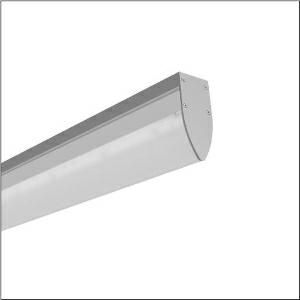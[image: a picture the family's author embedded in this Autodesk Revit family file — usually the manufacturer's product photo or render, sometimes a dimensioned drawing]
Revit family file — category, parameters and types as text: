
# Revit family: mira_r__21_td_51fr527d424a_f4a9
name_source: partatom
category: Lighting Fixtures
units: mm (PartAtom-declared; Revit-internal decimal feet)

## family parameters
Cut with Voids When Loaded = No
Host = Face
Light Source = No
Part Type = Normal
Room Calculation Point = No
Round Connector Dimension = Use Diameter
Shared = No

## types (1)
- Mira® 21 TD (1 x LED, 2020 lm, 14 W, 4000K)
    Apparent Load = 14 VA
    CIE Flux Codes = 40 68 87 81 100
    Color Rendering = 80
    Color Temperature = 4000K
    Default Elevation = 1800 mm
    Description = Mira® 21 TD, clean room luminaire, primary light control with reflector, primary optical cover: cover, of PMMA, frosted, light emission: direct distribution, primary light characteristic: symmetric, installation type: surface-mounted, LED, rated luminous flux: 2.020lm, luminous efficacy: 144lm/W, light colour: 840, colour temperature: 4000K, control gear: ON/OFF, with terminal, 3-pole, max. 2.5mm², mains connection: 230V, AC, 50/60Hz, rated input power: 14W, luminaire housing, of sheet steel, coated, pure white (RAL 9010), length: 600mm, width: 55mm, height: 120mm, protection rating (complete): IP43, insulation class (complete): insulation class I (protective earthing), certification: CE, UKCA, permissible operating ambient temperature: -5..+40°C, standard: EN 50419, packaging unit: 1 piece
    Height = 120 mm
    Lamp = 1 x LED
    Lamp Light Flux = 2020 lm
    Lamp Power = 14 W
    Lamp count = 1
    Length = 600 mm
    Luminous efficacy = 144 lm/W
    Manufacturer = Siteco
    ModVariant = No
    Model = 51FR527D424A
    Mounting Place = Ceiling
    Mounting Type = Surface mounted
    Number of Poles = 1
    OnlyDefault = Yes
    Power Factor = 1
    Product Name = Mira® 21 TD
    Product group = clean room luminaire | ceiling mounted
    ProductGroupID = 305
    Protection Class = Protection class I
    Protection Degree = IP 43
    RLX_Detail_Level = 1
    RLX_Emergency_Light_Flux = 0 lm
    RLX_Emergency_Type = 0
    RLX_Emergency_Type_DB = No
    RlxData = <blob elided: 25869 chars, md5=cd2b4e9b>
    Socket = socket
    Standby Power = 0 W
    System Light Flux = 2020 lm
    System Power = 14 W
    Type Comments = Product without accessories
    Type Image = l_1007115.jpg
    URL = http://relux.com
    VarID = ---
    Voltage = 0 V
    Weight = 0.00 kg
    Width = 55 mm

## geometry (parser evidence)
native form markers: Blend x4, Sweep x12
no freeform markers — native parametric forms only
